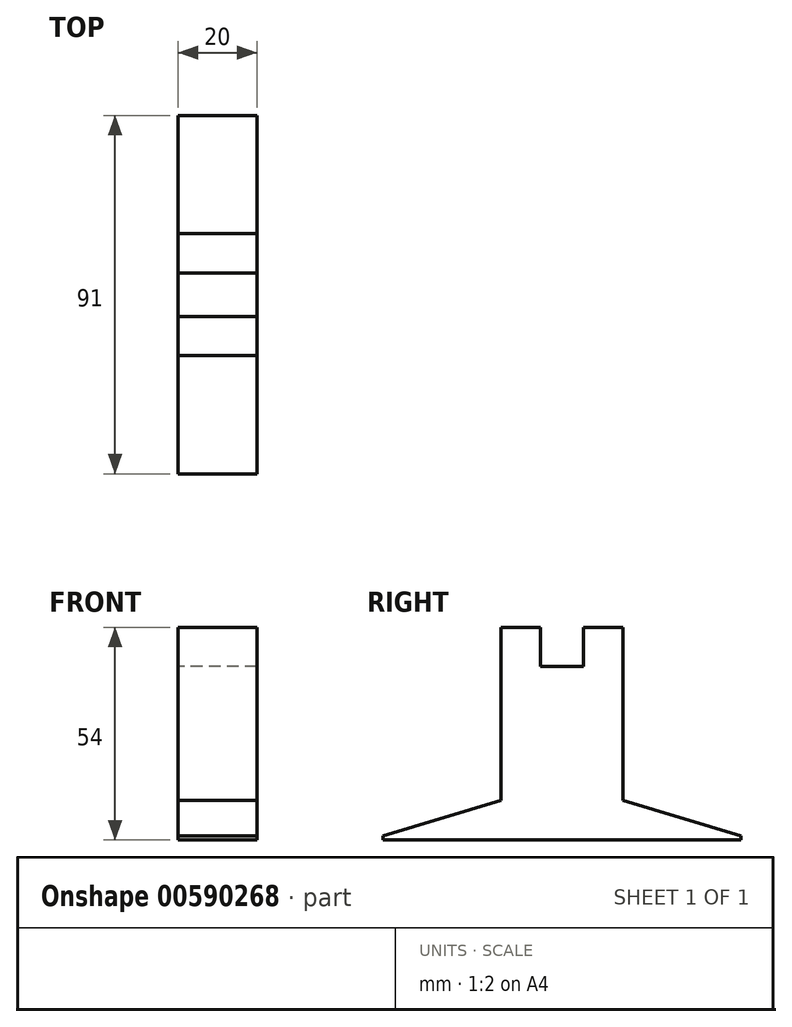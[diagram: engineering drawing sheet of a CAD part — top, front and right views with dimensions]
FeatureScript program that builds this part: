
annotation { "Feature Type Name" : "Feature", "Feature Type Description" : "" }
export const myFeature = defineFeature(function(context is Context, id is Id, definition is map)
    precondition{}
    {
        {
            var Q0;
            Q0=qCreatedBy(makeId("Top.planeOp"),FACE);
            var sketch = newSketch(context, id + "F0", { "sketchPlane" : qUnion([Q0])});
            skLineSegment(sketch, "E0.bottom", {"start": v(0, 0) * mm, "end": v(20, 0) * mm});
            skLineSegment(sketch, "E0.top", {"start": v(0, 31) * mm, "end": v(20, 31) * mm});
            skLineSegment(sketch, "E0.left", {"start": v(0, 0) * mm, "end": v(0, 31) * mm});
            skLineSegment(sketch, "E0.right", {"start": v(20, 0) * mm, "end": v(20, 31) * mm});
            skSolve(sketch);
        }
        {
            var Q0;
            Q0=qSketchRegion(id+"F0",true);
            extrude(context, id + "F1", {"entities" : qUnion([Q0]), "depth" : 44 * mm, "offsetDistance" : 25 * mm});
        }
        {
            var Q0;
            Q0=makeQuery(id+"F1.opExtrude","CAP_FACE",FACE,{"disambiguationData":[OSD([sQuery(id+"F0.wireOp",EDGE,"E0.bottom"),sQuery(id+"F0.wireOp",EDGE,"E0.top"),sQuery(id+"F0.wireOp",EDGE,"E0.left"),sQuery(id+"F0.wireOp",EDGE,"E0.right")])],"isStart":false});
            var sketch = newSketch(context, id + "F2", { "sketchPlane" : qUnion([Q0])});
            skLineSegment(sketch, "E1.bottom", {"start": v(0, 31) * mm, "end": v(20, 31) * mm});
            skLineSegment(sketch, "E1.top", {"start": v(0, 21) * mm, "end": v(20, 21) * mm});
            skLineSegment(sketch, "E1.left", {"start": v(0, 31) * mm, "end": v(0, 21) * mm});
            skLineSegment(sketch, "E1.right", {"start": v(20, 31) * mm, "end": v(20, 21) * mm});
            skLineSegment(sketch, "E2.bottom", {"start": v(20, 0) * mm, "end": v(0, 0) * mm});
            skLineSegment(sketch, "E2.top", {"start": v(20, 10) * mm, "end": v(0, 10) * mm});
            skLineSegment(sketch, "E2.left", {"start": v(20, 0) * mm, "end": v(20, 10) * mm});
            skLineSegment(sketch, "E2.right", {"start": v(0, 0) * mm, "end": v(0, 10) * mm});
            skSolve(sketch);
        }
        {
            var Q0;
            Q0=qSketchRegion(id+"F2",true);
            extrude(context, id + "F3", {"entities" : qUnion([Q0]), "operationType" : NewBodyOperationType.ADD, "depth" : 10 * mm, "offsetDistance" : 25 * mm});
        }
        {
            var Q0;
            Q0=makeQuery(id+"F3.boolean.opBoolean","MERGE",FACE,{"derivedFrom":[makeQuery(id+"F1.opExtrude","SWEPT_FACE",FACE,{"disambiguationData":[OSD([sQuery(id+"F0.wireOp",EDGE,"E0.bottom")])]}),makeQuery(id+"F3.opExtrude","SWEPT_FACE",FACE,{"disambiguationData":[OSD([sQuery(id+"F2.wireOp",EDGE,"E2.bottom")])]})]});
            var sketch = newSketch(context, id + "F4", { "sketchPlane" : qUnion([Q0])});
            skLineSegment(sketch, "E3.bottom", {"start": v(0, 0) * mm, "end": v(20, 0) * mm});
            skLineSegment(sketch, "E3.top", {"start": v(0, 10) * mm, "end": v(20, 10) * mm});
            skLineSegment(sketch, "E3.left", {"start": v(0, 0) * mm, "end": v(0, 10) * mm});
            skLineSegment(sketch, "E3.right", {"start": v(20, 0) * mm, "end": v(20, 10) * mm});
            skSolve(sketch);
        }
        {
            var Q0;
            Q0=qSketchRegion(id+"F4",true);
            extrude(context, id + "F5", {"entities" : qUnion([Q0]), "operationType" : NewBodyOperationType.ADD, "depth" : 30 * mm, "offsetDistance" : 25 * mm});
        }
        {
            var Q0;
            Q0=makeQuery(id+"F3.boolean.opBoolean","MERGE",FACE,{"derivedFrom":[makeQuery(id+"F1.opExtrude","SWEPT_FACE",FACE,{"disambiguationData":[OSD([sQuery(id+"F0.wireOp",EDGE,"E0.top")])]}),makeQuery(id+"F3.opExtrude","SWEPT_FACE",FACE,{"disambiguationData":[OSD([sQuery(id+"F2.wireOp",EDGE,"E1.bottom")])]})]});
            var sketch = newSketch(context, id + "F6", { "sketchPlane" : qUnion([Q0])});
            skLineSegment(sketch, "E4.bottom", {"start": v(-20, 0) * mm, "end": v(0, 0) * mm});
            skLineSegment(sketch, "E4.top", {"start": v(-20, 10) * mm, "end": v(0, 10) * mm});
            skLineSegment(sketch, "E4.left", {"start": v(-20, 0) * mm, "end": v(-20, 10) * mm});
            skLineSegment(sketch, "E4.right", {"start": v(0, 0) * mm, "end": v(0, 10) * mm});
            skSolve(sketch);
        }
        {
            var Q0;
            Q0=qSketchRegion(id+"F6",true);
            extrude(context, id + "F7", {"entities" : qUnion([Q0]), "operationType" : NewBodyOperationType.ADD, "depth" : 30 * mm, "offsetDistance" : 25 * mm});
        }
        {
            var Q0;
            Q0=makeQuery(id+"F7.boolean.opBoolean","MERGE",FACE,{"derivedFrom":[makeQuery(id+"F5.boolean.opBoolean","MERGE",FACE,{"derivedFrom":[makeQuery(id+"F3.boolean.opBoolean","MERGE",FACE,{"derivedFrom":[makeQuery(id+"F1.opExtrude","SWEPT_FACE",FACE,{"disambiguationData":[OSD([sQuery(id+"F0.wireOp",EDGE,"E0.right")])]}),makeQuery(id+"F3.opExtrude","SWEPT_FACE",FACE,{"disambiguationData":[OSD([sQuery(id+"F2.wireOp",EDGE,"E1.right")])]}),makeQuery(id+"F3.opExtrude","SWEPT_FACE",FACE,{"disambiguationData":[OSD([sQuery(id+"F2.wireOp",EDGE,"E2.left")])]})]}),makeQuery(id+"F5.opExtrude","SWEPT_FACE",FACE,{"disambiguationData":[OSD([sQuery(id+"F4.wireOp",EDGE,"E3.right")])]})]}),makeQuery(id+"F7.opExtrude","SWEPT_FACE",FACE,{"disambiguationData":[OSD([sQuery(id+"F6.wireOp",EDGE,"E4.left")])]})]});
            var sketch = newSketch(context, id + "F8", { "sketchPlane" : qUnion([Q0])});
            skLineSegment(sketch, "E5", {"start": v(0, 10) * mm, "end": v(-30, 1) * mm});
            skLineSegment(sketch, "E6", {"start": v(-30, 1) * mm, "end": v(-30, 10) * mm});
            skLineSegment(sketch, "E7", {"start": v(-30, 10) * mm, "end": v(0, 10) * mm});
            skLineSegment(sketch, "E8", {"start": v(31, 10) * mm, "end": v(61, 10) * mm});
            skLineSegment(sketch, "E9", {"start": v(61, 10) * mm, "end": v(61, 1) * mm});
            skLineSegment(sketch, "E10", {"start": v(61, 1) * mm, "end": v(31, 10) * mm});
            skSolve(sketch);
        }
        {
            var Q0;
            Q0=makeQuery(id+"F8.imprint","IMPRINT",FACE,{"disambiguationData":[TD([[makeQuery(id+"F8.imprint","IMPRINT",EDGE,{"derivedFrom":sQuery(id+"F8.wireOp",EDGE,"E5")}),-1.0]])]});
            var Q1;
            Q1=makeQuery(id+"F8.imprint","IMPRINT",FACE,{"disambiguationData":[TD([[makeQuery(id+"F8.imprint","IMPRINT",EDGE,{"derivedFrom":sQuery(id+"F8.wireOp",EDGE,"E8")}),1.0]])]});
            extrude(context, id + "F9", {"entities" : qUnion([Q0, Q1]), "operationType" : NewBodyOperationType.REMOVE, "oppositeDirection" : true, "depth" : 20 * mm, "offsetDistance" : 25 * mm});
        }
    });
